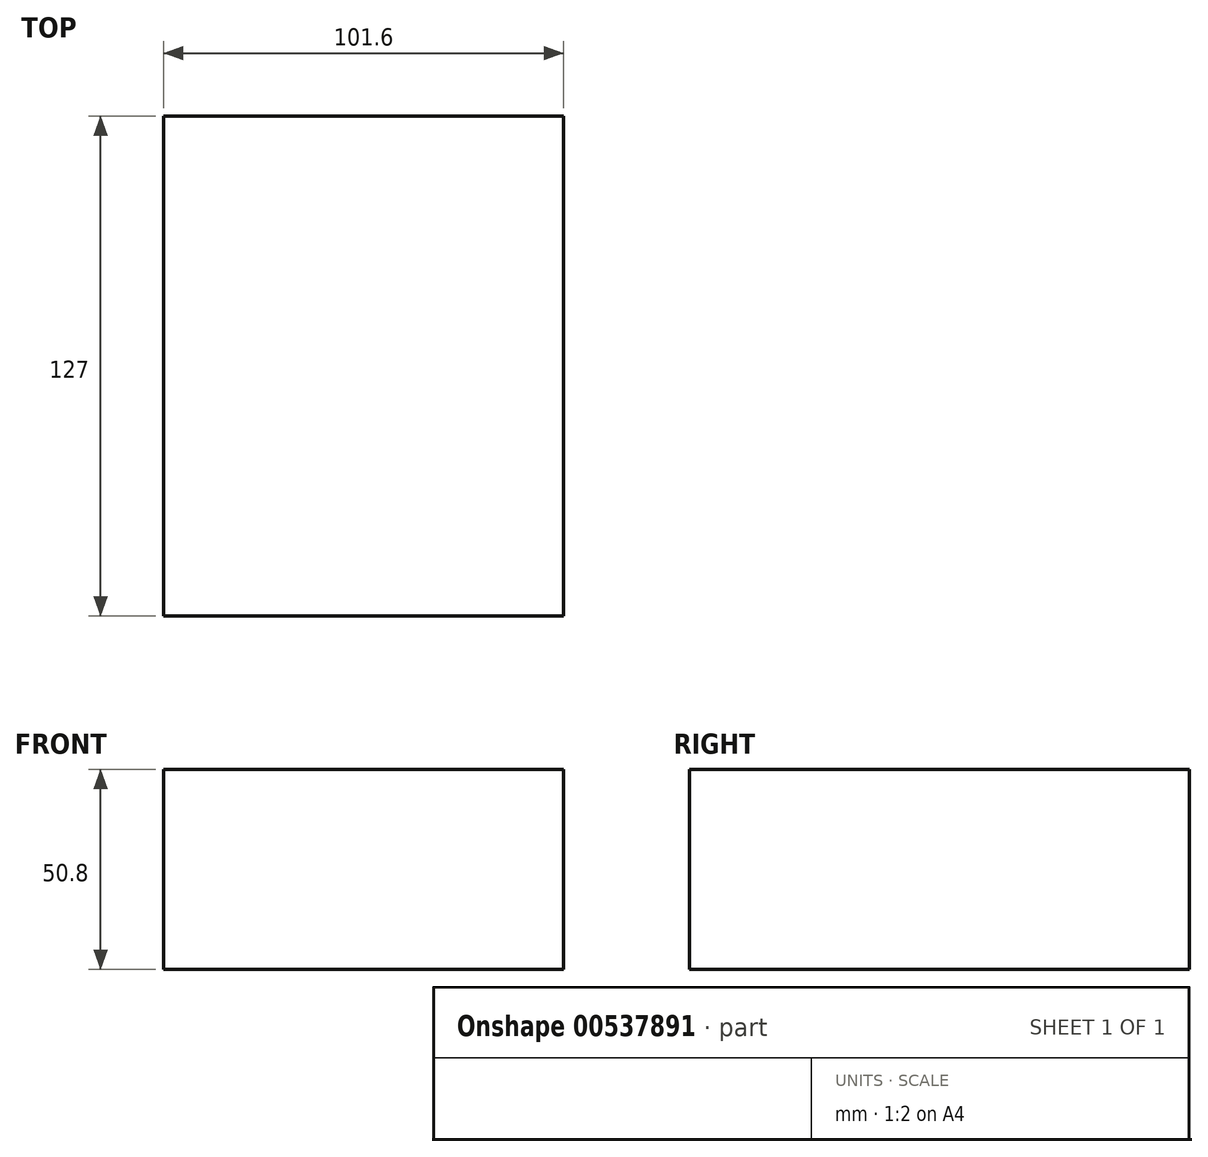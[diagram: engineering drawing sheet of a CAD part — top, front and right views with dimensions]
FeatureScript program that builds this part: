
annotation { "Feature Type Name" : "Feature", "Feature Type Description" : "" }
export const myFeature = defineFeature(function(context is Context, id is Id, definition is map)
    precondition{}
    {
        {
            var Q0;
            Q0=qCreatedBy(makeId("Front.planeOp"),FACE);
            var sketch = newSketch(context, id + "F0", { "sketchPlane" : qUnion([Q0])});
            skLineSegment(sketch, "E0.bottom", {"start": v(50.8, 25.4) * mm, "end": v(-50.8, 25.4) * mm});
            skLineSegment(sketch, "E0.top", {"start": v(50.8, -25.4) * mm, "end": v(-50.8, -25.4) * mm});
            skLineSegment(sketch, "E0.left", {"start": v(50.8, 25.4) * mm, "end": v(50.8, -25.4) * mm});
            skLineSegment(sketch, "E0.right", {"start": v(-50.8, 25.4) * mm, "end": v(-50.8, -25.4) * mm});
            skPoint(sketch, "E0.middle", {"position": v(0, 0) * mm});
            skSolve(sketch);
        }
        {
            var Q0;
            Q0 = qSketchRegion(id + "F0", true);
            extrude(context, id + "F1", {"entities" : qUnion([Q0]), "endBound" : BoundingType.SYMMETRIC, "depth" : 127 * mm, "offsetDistance" : 25.4 * mm});
        }
    });
